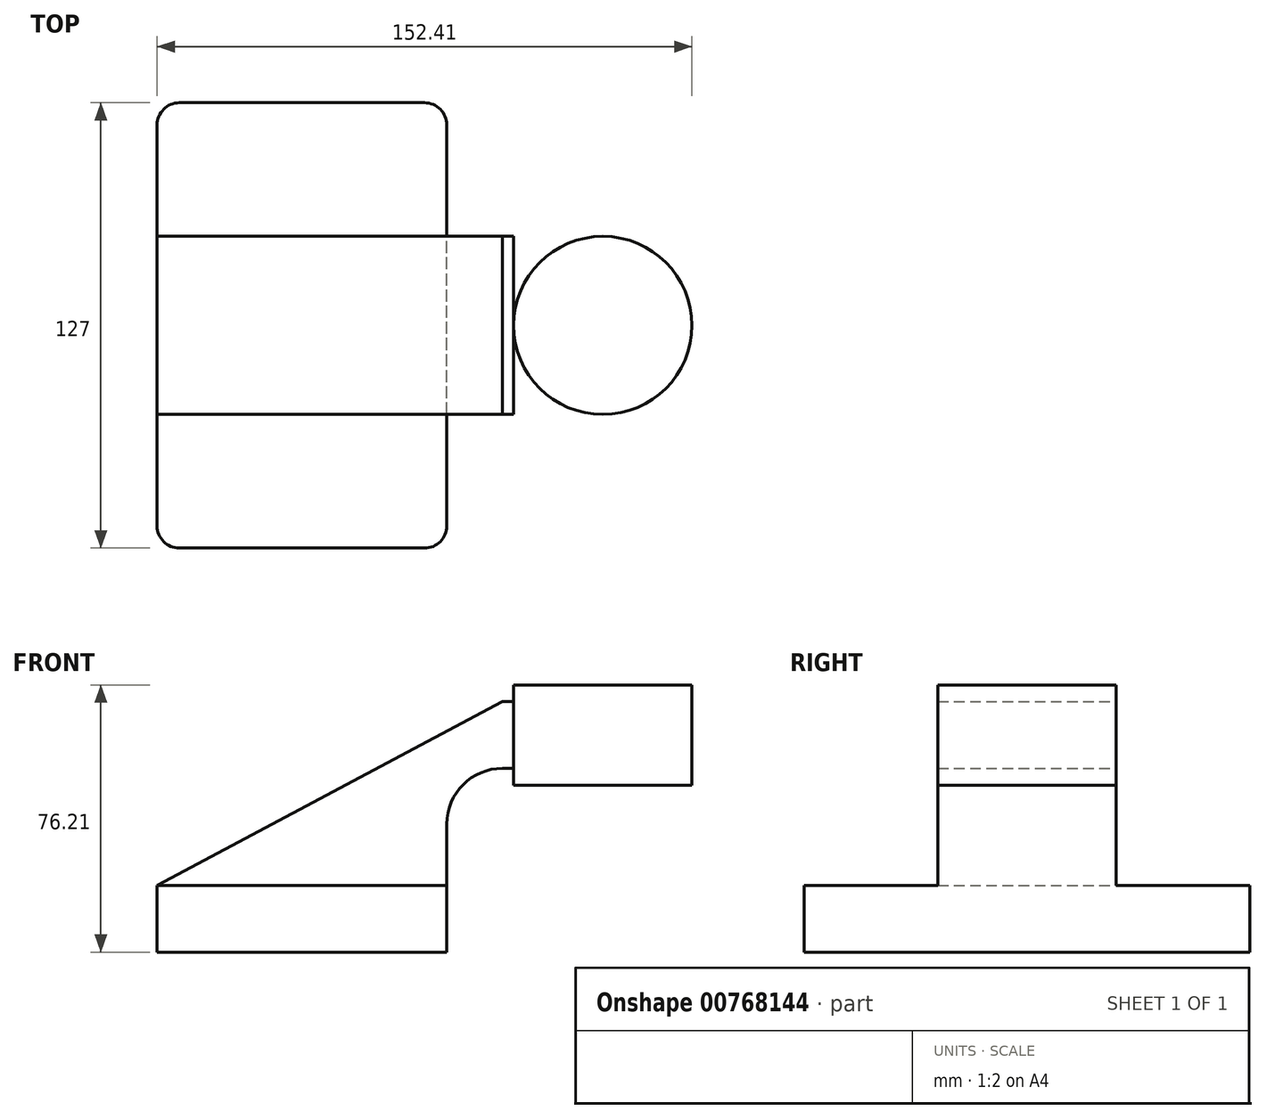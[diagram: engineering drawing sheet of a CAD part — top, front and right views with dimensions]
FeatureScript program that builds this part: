
annotation { "Feature Type Name" : "Feature", "Feature Type Description" : "" }
export const myFeature = defineFeature(function(context is Context, id is Id, definition is map)
    precondition{}
    {
        {
            var Q0;
            Q0=qCreatedBy(makeId("Front.planeOp"),FACE);
            var sketch = newSketch(context, id + "F0", { "sketchPlane" : qUnion([Q0])});
            skLineSegment(sketch, "E0.bottom", {"start": v(-41.28, 9.52) * mm, "end": v(41.28, 9.52) * mm});
            skLineSegment(sketch, "E0.top", {"start": v(-41.28, -9.52) * mm, "end": v(41.28, -9.52) * mm});
            skLineSegment(sketch, "E0.left", {"start": v(-41.28, 9.52) * mm, "end": v(-41.28, -9.52) * mm});
            skLineSegment(sketch, "E0.right", {"start": v(41.28, 9.52) * mm, "end": v(41.28, -9.52) * mm});
            skPoint(sketch, "E0.middle", {"position": v(0, 0) * mm});
            skLineSegment(sketch, "E1.bottom", {"start": v(60.33, 66.68) * mm, "end": v(111.13, 66.68) * mm});
            skLineSegment(sketch, "E1.top", {"start": v(60.33, 38.1) * mm, "end": v(111.13, 38.1) * mm});
            skLineSegment(sketch, "E1.left", {"start": v(60.33, 66.68) * mm, "end": v(60.33, 38.1) * mm});
            skLineSegment(sketch, "E1.right", {"start": v(111.13, 66.68) * mm, "end": v(111.13, 38.1) * mm});
            skPoint(sketch, "E1.middle", {"position": v(85.73, 52.39) * mm});
            skLineSegment(sketch, "E2", {"start": v(41.28, 9.52) * mm, "end": v(41.28, 27) * mm});
            skArc(sketch, "E3", {"start": v(41.27, 27) * mm, "mid": v(45.92, 38.23) * mm, "end": v(57.15, 42.88) * mm});
            skLineSegment(sketch, "E4", {"start": v(57.15, 42.88) * mm, "end": v(85.72, 42.88) * mm});
            skLineSegment(sketch, "E5", {"start": v(85.72, 42.88) * mm, "end": v(80.57, 42.88) * mm});
            skLineSegment(sketch, "E6.0", {"start": v(57.15, 61.93) * mm, "end": v(85.72, 61.93) * mm});
            skArc(sketch, "E6.1", {"start": v(22.23, 27) * mm, "mid": v(32.45, 51.7) * mm, "end": v(57.15, 61.93) * mm});
            skLineSegment(sketch, "E6.2", {"start": v(22.23, 9.52) * mm, "end": v(22.23, 27) * mm});
            skLineSegment(sketch, "E7", {"start": v(85.73, 66.68) * mm, "end": v(85.73, 38.1) * mm});
            skFitSpline(sketch, "E8", {"points": [v(-41.28, 9.52) * mm, v(57.15, 61.93) * mm], "startDerivative": vector(98.43, 52.4) * mm, "endDerivative": vector(98.43, 52.4) * mm});
            skSolve(sketch);
        }
        {
            var Q0;
            Q0=makeQuery(id+"F0.imprint","IMPRINT",FACE,{"disambiguationData":[TD([[makeQuery(id+"F0.imprint","IMPRINT",EDGE,{"derivedFrom":sQuery(id+"F0.wireOp",EDGE,"E0.top")}),1.0]])]});
            extrude(context, id + "F1", {"entities" : qUnion([Q0]), "endBound" : BoundingType.SYMMETRIC, "depth" : 127 * mm, "offsetDistance" : 25.4 * mm});
        }
        {
            var Q0;
            {var subQ5=sQuery(id+"F0.wireOp",EDGE,"E5");Q0=makeQuery(id+"F0.imprint","IMPRINT",FACE,{"disambiguationData":[TD([[makeQuery(id+"F0.imprint","IMPRINT",EDGE,{"derivedFrom":subQ5}),-1.0]])]});}
            var Q1;
            {var subQ1=sQuery(id+"F0.wireOp",EDGE,"E2");Q1=makeQuery(id+"F0.imprint","IMPRINT",FACE,{"disambiguationData":[TD([[makeQuery(id+"F0.imprint","IMPRINT",EDGE,{"derivedFrom":subQ1}),1.0]])]});}
            var Q2;
            {var subQ0=sQuery(id+"F0.wireOp",EDGE,"E8");var subQ1=sQuery(id+"F0.wireOp",EDGE,"E6.1");var subQ3=makeQuery(id+"F0.imprint","INTERSECT",VERTEX,{"derivedFrom":[subQ1,subQ0]});Q2=makeQuery(id+"F0.imprint","IMPRINT",FACE,{"disambiguationData":[TD([[makeQuery(id+"F0.imprint","IMPRINT",EDGE,{"disambiguationData":[TD([[subQ3,-1.0]])],"derivedFrom":subQ1}),-1.0]])]});}
            extrude(context, id + "F2", {"entities" : qUnion([Q0, Q1, Q2]), "operationType" : NewBodyOperationType.ADD, "endBound" : BoundingType.SYMMETRIC, "depth" : 50.8 * mm, "offsetDistance" : 25.4 * mm});
        }
        {
            var Q0;
            {var subQ3=sQuery(id+"F0.wireOp",EDGE,"E6.2");Q0=makeQuery(id+"F0.imprint","IMPRINT",FACE,{"disambiguationData":[TD([[makeQuery(id+"F0.imprint","IMPRINT",EDGE,{"derivedFrom":subQ3}),1.0]])]});}
            extrude(context, id + "F3", {"entities" : qUnion([Q0]), "operationType" : NewBodyOperationType.ADD, "endBound" : BoundingType.SYMMETRIC, "depth" : 15.88 * mm, "offsetDistance" : 25.4 * mm});
        }
        {
            var Q0;
            {var subQ0=sQuery(id+"F0.wireOp",EDGE,"E1.right");Q0=makeQuery(id+"F0.imprint","IMPRINT",FACE,{"disambiguationData":[TD([[makeQuery(id+"F0.imprint","IMPRINT",EDGE,{"derivedFrom":subQ0}),-1.0]])]});}
            var Q1;
            Q1=sQuery(id+"F0.wireOp",EDGE,"E7");
            revolve(context, id + "F4", {"operationType" : NewBodyOperationType.ADD, "surfaceOperationType" : NewSurfaceOperationType.NEW, "entities" : qUnion([Q0]), "axis" : qUnion([Q1]), "revolveType" : RevolveType.FULL});
        }
        {
            var Q0;
            Q0=makeQuery(id+"F1.opExtrude","CAP_EDGE",EDGE,{"disambiguationData":[OSD([sQuery(id+"F0.wireOp",EDGE,"E0.left")])],"isStart":false});
            var Q1;
            Q1=makeQuery(id+"F1.opExtrude","CAP_EDGE",EDGE,{"disambiguationData":[OSD([sQuery(id+"F0.wireOp",EDGE,"E0.right")])],"isStart":false});
            var Q2;
            Q2=makeQuery(id+"F1.opExtrude","CAP_EDGE",EDGE,{"disambiguationData":[OSD([sQuery(id+"F0.wireOp",EDGE,"E0.right")])],"isStart":true});
            var Q3;
            Q3=makeQuery(id+"F1.opExtrude","CAP_EDGE",EDGE,{"disambiguationData":[OSD([sQuery(id+"F0.wireOp",EDGE,"E0.left")])],"isStart":true});
            fillet(context, id + "F5", {"entities" : qUnion([Q0, Q1, Q2, Q3]), "radius" : 6.35 * mm, "tangentPropagation" : true, "allowEdgeOverflow" : false});
        }
    });
